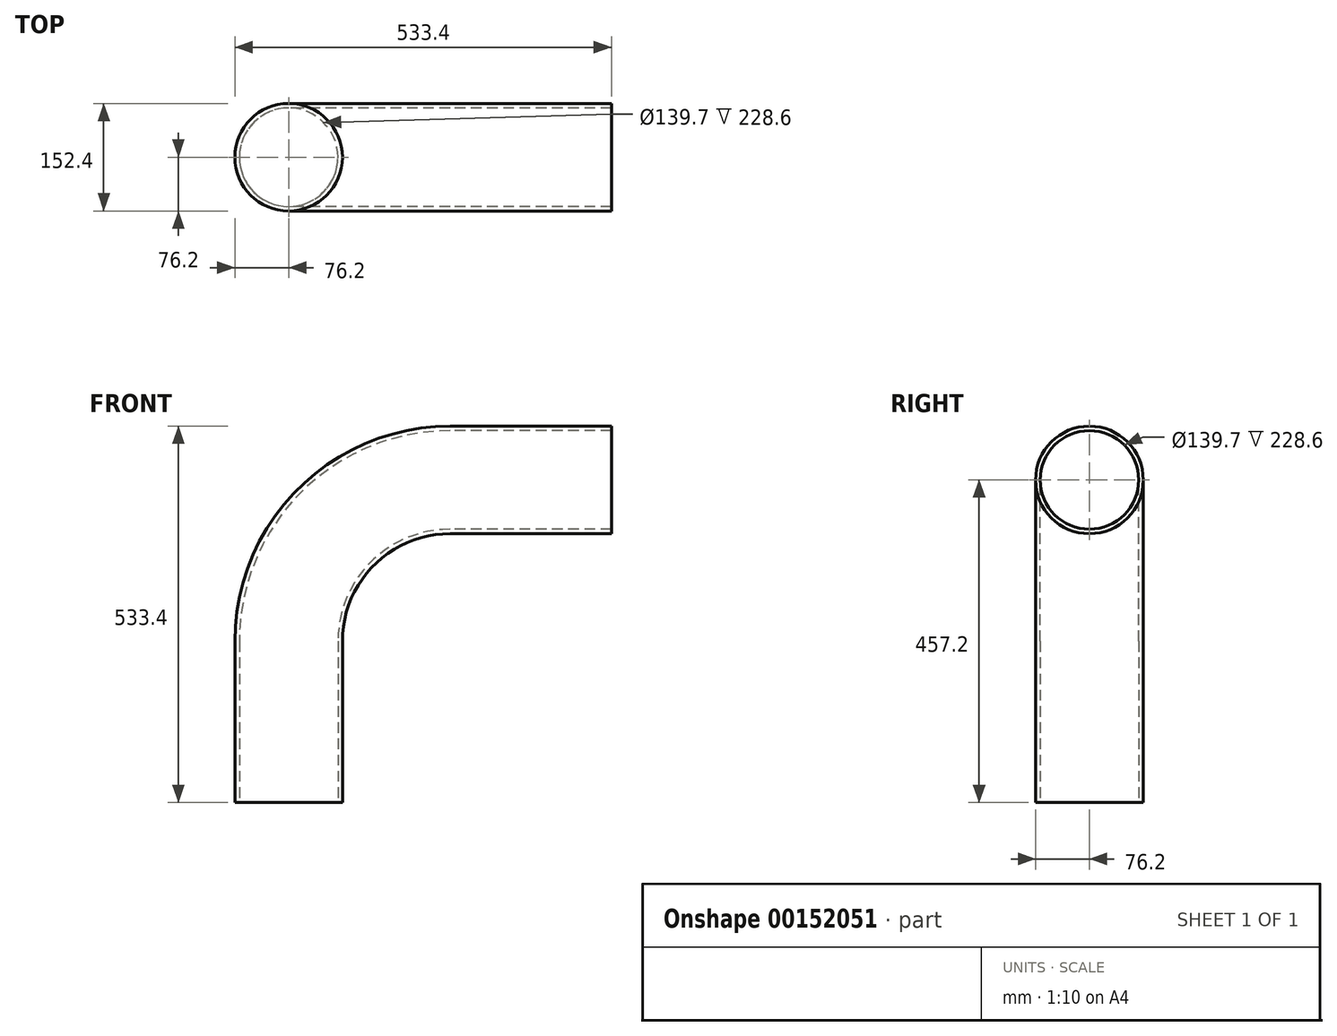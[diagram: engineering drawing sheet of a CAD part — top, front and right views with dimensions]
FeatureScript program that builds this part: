
annotation { "Feature Type Name" : "Feature", "Feature Type Description" : "" }
export const myFeature = defineFeature(function(context is Context, id is Id, definition is map)
    precondition{}
    {
        {
            var Q0;
            Q0=qCreatedBy(makeId("Front.planeOp"),FACE);
            var sketch = newSketch(context, id + "F0", { "sketchPlane" : qUnion([Q0])});
            skLineSegment(sketch, "E0", {"start": v(0, 0) * mm, "end": v(-76.2, 0) * mm});
            skLineSegment(sketch, "E1", {"start": v(-76.2, 0) * mm, "end": v(-76.2, 228.6) * mm});
            skLineSegment(sketch, "E2", {"start": v(228.6, 533.4) * mm, "end": v(457.2, 533.4) * mm});
            skLineSegment(sketch, "E3", {"start": v(457.2, 533.4) * mm, "end": v(457.2, 381) * mm});
            skLineSegment(sketch, "E4", {"start": v(0, 0) * mm, "end": v(76.2, 0) * mm});
            skLineSegment(sketch, "E5", {"start": v(76.2, 0) * mm, "end": v(76.2, 228.6) * mm});
            skLineSegment(sketch, "E6", {"start": v(228.6, 381) * mm, "end": v(457.2, 381) * mm});
            skPoint(sketch, "E7.visualSharp", {"position": v(76.2, 381) * mm});
            skArc(sketch, "E7.filletArc", {"start": v(228.6, 381) * mm, "mid": v(120.84, 336.36) * mm, "end": v(76.2, 228.6) * mm});
            skPoint(sketch, "E8.visualSharp", {"position": v(-76.2, 533.4) * mm});
            skArc(sketch, "E8.filletArc", {"start": v(228.6, 533.4) * mm, "mid": v(13.07, 444.13) * mm, "end": v(-76.2, 228.6) * mm});
            skSolve(sketch);
        }
        {
            var Q0;
            Q0 = qSketchRegion(id + "F0", true);
            extrude(context, id + "F1", {"entities" : qUnion([Q0]), "depth" : 152.4 * mm});
        }
        {
            var Q0;
            Q0=makeQuery(id+"F1.opExtrude","CAP_EDGE",EDGE,{"disambiguationData":[OSD([sQuery(id+"F0.wireOp",EDGE,"E8.filletArc")])],"isStart":false});
            var Q1;
            Q1=makeQuery(id+"F1.opExtrude","CAP_EDGE",EDGE,{"disambiguationData":[OSD([sQuery(id+"F0.wireOp",EDGE,"E7.filletArc")])],"isStart":false});
            var Q2;
            Q2=makeQuery(id+"F1.opExtrude","CAP_EDGE",EDGE,{"disambiguationData":[OSD([sQuery(id+"F0.wireOp",EDGE,"E7.filletArc")])],"isStart":true});
            var Q3;
            Q3=makeQuery(id+"F1.opExtrude","CAP_EDGE",EDGE,{"disambiguationData":[OSD([sQuery(id+"F0.wireOp",EDGE,"E8.filletArc")])],"isStart":true});
            fillet(context, id + "F2", {"entities" : qUnion([Q0, Q1, Q2, Q3]), "radius" : 76.2 * mm, "tangentPropagation" : true, "allowEdgeOverflow" : false});
        }
        {
            var Q0;
            Q0=makeQuery(id+"F1.opExtrude","SWEPT_FACE",FACE,{"disambiguationData":[OSD([sQuery(id+"F0.wireOp",EDGE,"E0"),sQuery(id+"F0.wireOp",EDGE,"E4")])]});
            var Q1;
            Q1=makeQuery(id+"F1.opExtrude","SWEPT_FACE",FACE,{"disambiguationData":[OSD([sQuery(id+"F0.wireOp",EDGE,"E3")])]});
            shell(context, id + "F3", {"entities" : qUnion([Q0, Q1]), "thickness" : 6.35 * mm});
        }
    });
